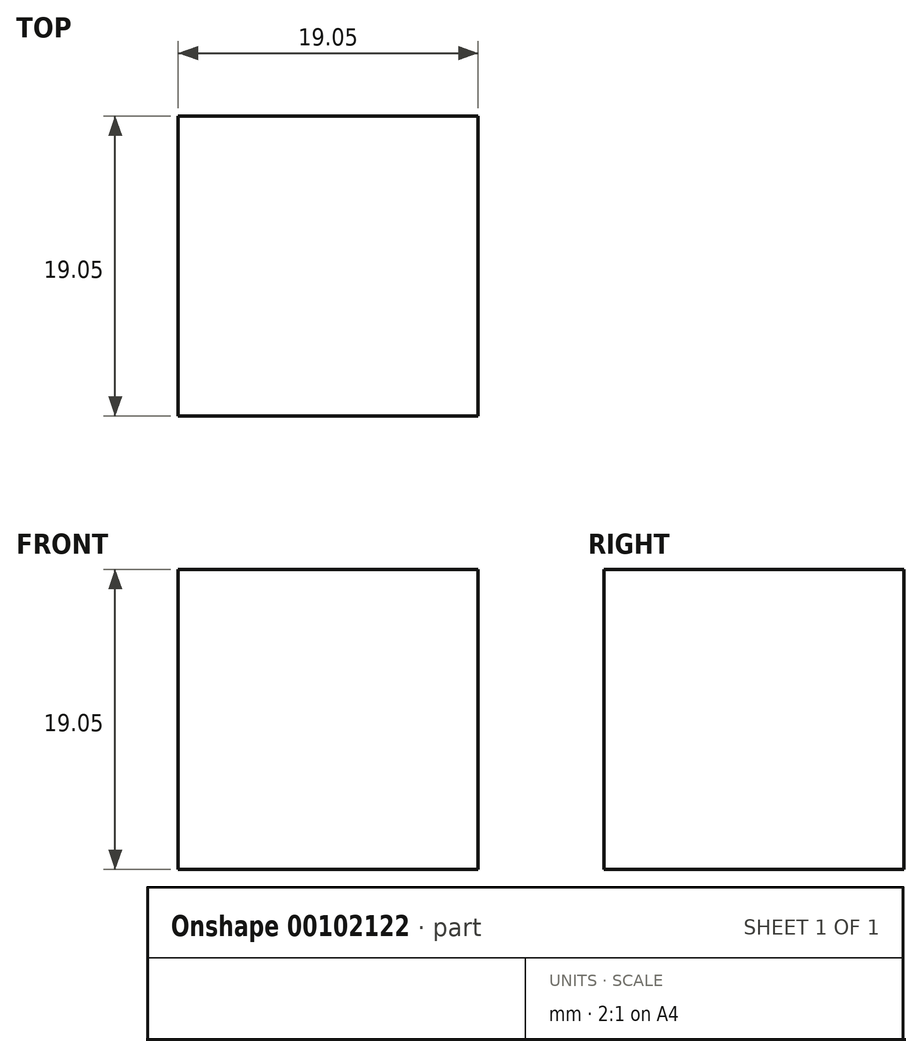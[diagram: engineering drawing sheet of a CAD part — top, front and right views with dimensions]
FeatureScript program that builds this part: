
annotation { "Feature Type Name" : "Feature", "Feature Type Description" : "" }
export const myFeature = defineFeature(function(context is Context, id is Id, definition is map)
    precondition{}
    {
        {
            var Q0;
            Q0=qCreatedBy(makeId("Top.planeOp"),FACE);
            var sketch = newSketch(context, id + "F0", { "sketchPlane" : qUnion([Q0])});
            skLineSegment(sketch, "E0.bottom", {"start": v(-0.26, 0.96) * mm, "end": v(18.79, 0.96) * mm});
            skLineSegment(sketch, "E0.top", {"start": v(-0.26, -18.09) * mm, "end": v(18.79, -18.09) * mm});
            skLineSegment(sketch, "E0.left", {"start": v(-0.26, 0.96) * mm, "end": v(-0.26, -18.09) * mm});
            skLineSegment(sketch, "E0.right", {"start": v(18.79, 0.96) * mm, "end": v(18.79, -18.09) * mm});
            skSolve(sketch);
        }
        {
            var Q0;
            Q0 = qSketchRegion(id + "F0", true);
            extrude(context, id + "F1", {"entities" : qUnion([Q0]), "depth" : 19.05 * mm});
        }
    });
